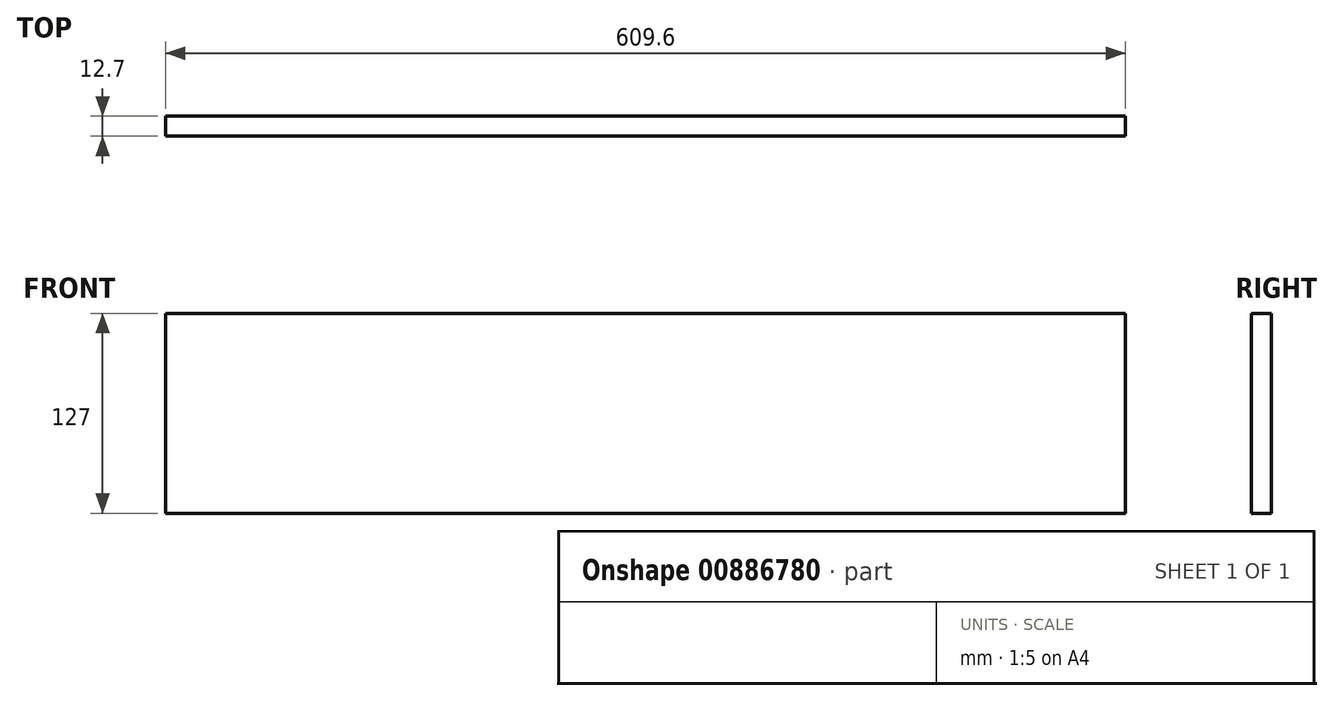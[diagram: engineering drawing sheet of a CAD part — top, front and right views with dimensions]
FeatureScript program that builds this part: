
annotation { "Feature Type Name" : "Feature", "Feature Type Description" : "" }
export const myFeature = defineFeature(function(context is Context, id is Id, definition is map)
    precondition{}
    {
        {
            var Q0;
            Q0=qCreatedBy(makeId("Front.planeOp"),FACE);
            var sketch = newSketch(context, id + "F0", { "sketchPlane" : qUnion([Q0])});
            skLineSegment(sketch, "E0.bottom", {"start": v(-304.8, 63.5) * mm, "end": v(304.8, 63.5) * mm});
            skLineSegment(sketch, "E0.top", {"start": v(-304.8, -63.5) * mm, "end": v(304.8, -63.5) * mm});
            skLineSegment(sketch, "E0.left", {"start": v(-304.8, 63.5) * mm, "end": v(-304.8, -63.5) * mm});
            skLineSegment(sketch, "E0.right", {"start": v(304.8, 63.5) * mm, "end": v(304.8, -63.5) * mm});
            skPoint(sketch, "E0.middle", {"position": v(0, 0) * mm});
            skSolve(sketch);
        }
        {
            var Q0;
            Q0=makeQuery(id+"F0.imprint","IMPRINT",FACE,{"disambiguationData":[TD([[makeQuery(id+"F0.imprint","IMPRINT",EDGE,{"derivedFrom":sQuery(id+"F0.wireOp",EDGE,"E0.bottom")}),-1.0]])]});
            extrude(context, id + "F1", {"entities" : qUnion([Q0]), "depth" : 12.7 * mm, "offsetDistance" : 25.4 * mm});
        }
    });
